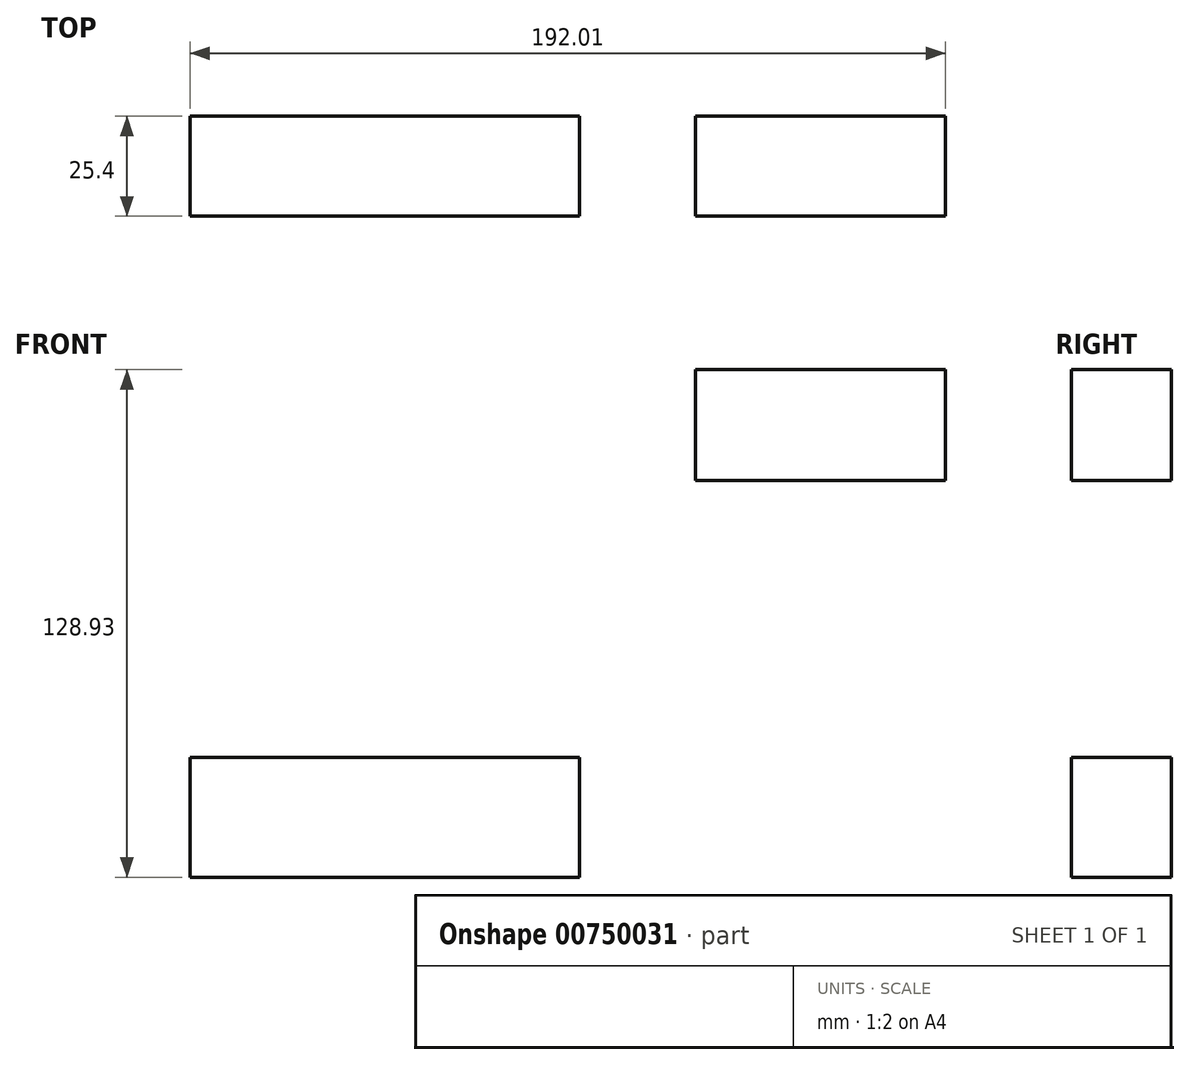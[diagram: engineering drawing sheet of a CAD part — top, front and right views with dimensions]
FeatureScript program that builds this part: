
annotation { "Feature Type Name" : "Feature", "Feature Type Description" : "" }
export const myFeature = defineFeature(function(context is Context, id is Id, definition is map)
    precondition{}
    {
        {
            var Q0;
            Q0=qCreatedBy(makeId("Front.planeOp"),FACE);
            var sketch = newSketch(context, id + "F0", { "sketchPlane" : qUnion([Q0])});
            skLineSegment(sketch, "E0.bottom", {"start": v(49.48, -15.2) * mm, "end": v(-49.48, -15.2) * mm});
            skLineSegment(sketch, "E0.top", {"start": v(49.48, 15.2) * mm, "end": v(-49.48, 15.2) * mm});
            skLineSegment(sketch, "E0.left", {"start": v(49.48, -15.2) * mm, "end": v(49.48, 15.2) * mm});
            skLineSegment(sketch, "E0.right", {"start": v(-49.48, -15.2) * mm, "end": v(-49.48, 15.2) * mm});
            skPoint(sketch, "E0.middle", {"position": v(0, 0) * mm});
            skLineSegment(sketch, "E1.bottom", {"start": v(142.53, 85.58) * mm, "end": v(79.01, 85.58) * mm});
            skLineSegment(sketch, "E1.top", {"start": v(142.53, 113.72) * mm, "end": v(79.01, 113.72) * mm});
            skLineSegment(sketch, "E1.left", {"start": v(142.53, 85.58) * mm, "end": v(142.53, 113.72) * mm});
            skLineSegment(sketch, "E1.right", {"start": v(79.01, 85.58) * mm, "end": v(79.01, 113.72) * mm});
            skPoint(sketch, "E1.middle", {"position": v(110.77, 99.65) * mm});
            skSolve(sketch);
        }
        {
            var Q0;
            Q0 = qSketchRegion(id + "F0", true);
            extrude(context, id + "F1", {"entities" : qUnion([Q0]), "depth" : 25.4 * mm, "offsetDistance" : 25.4 * mm});
        }
    });
